# Revit family: Assa-Abloy_SecurityPortal_MP200_WallHosted
name_source: partatom
category: Doors
units: mm (PartAtom-declared; Revit-internal decimal feet)

## family parameters
Always vertical = Yes
Cut with Voids When Loaded = No
Host = Wall
OmniClass Number = 23.30.10.21.14
OmniClass Title = Security Doors
Room Calculation Point = No
Shared = No

## types (1)
- MP 200
    Access control/Biometrics = Yes
    AccessoryOptions = Contact manufacturer
    AlternativeDoorsetGlazing = Part of glazing spec
    Analytic Construction = <None>
    Anti-tailgating/Anti-piggybacking = Yes
    AntiFingerTrapRequirement = No
    BreakoutFacility = No
    Burglar resistance = EN 1627 class RC2/RC3
    CanopyHeightOptions = 250 - 1000 mm
    Capacity = 1 x 5 - 7
    Colour = Customer specific
    Configuration = 2 leafs
    Construction Type = Security Portal for controlled access
    Define Thermal Properties by = Schematic Type
    Description = Security Portal for controlled access, including high level TOF-3D sensor technology, burlgar resistance class RC2/RC3
    DiameterOptions = 1600-2500mm
    DoorIncluded = Yes
    DoorSeal = Yes
    DoorWingOptions = 2 wings
    DoorsetFasteners = Screws
    DoorsetOperation = Automatic
    DoorsetOptions = Sliding door system
    DrumWallOptions = Glass, Sandwich panel
    ElectronicLock = No
    Finish = Powder coated, Anodized, stainless steel, customer specific
    FireExit = No
    Frame Material = Aluminium
    FrameFinishOptions = Powder coated, Anodized, Clad in stainless steel, etc.
    FrameProfile = Aluminium
    FrameSeal = Yes
    Function = Exterior
    GlassLayers = 0
    GlassThickness1 = 10 mm  [stored 0.0328084 ft]
    GlassThickness2 = 10 mm  [stored 0.0328084 ft]
    GlassType = Part of glazing spec
    HandicapAccessible = Yes
    HasDrive = Yes
    HeightUnderCanopyOptions = Passage height: 2200 - 2600 mm
    Infiltration = 0
    IsExternal = Yes
    LeafColourOptions = All RAL, customer specific
    Manufacturer = Assa Abloy Entrance Systems
    ManufacturerURL = www.assaabloyentrance.com
    Material = Aluminium
    Model = Security Portal MP 200
    ModelReference = Depends on the configuration
    NominalHeight = 3250 mm
    NominalLength = 1800 mm  [stored 5.90551 ft]
    NominalWidth = 1800 mm  [stored 5.90551 ft]
    OperatingTemperature = -15º to +50ºC
    PassageWidthOptions = Depends on diameter, 1005 - 1619 mm
    ReferenceStandard = EN16005, EN16361, DIN 18650, etc.
    ReplacementCost = Depends on the configuration and door type
    SafetyDevices = Fully compliant with EN16005, Safety buffers, Presence sensors, etc.
    SelfClosing = Yes
    ServiceLifeDuration = 10-15 years
    Shape = Cylinder shaped
    SmokeStop = No
    ThermalTransmittance = 0
    ThresholdRequired = No
    ThresholdStripping = No
    URL = www.assaabloyentrance.com
    Uniclass2 = Ss_25_30_20_70
    Wall Closure = By host
    WarrantyDescription = Depends on country
    WarrantyDurationLabor = Depends on country
    WarrantyDurationParts = Depends on country
    WarrantyGuarantorLabor = Local door manufacturer
    WarrantyGuarantorParts = Local door manufacturer
    WarrantyStartDate = Depends on country
    Weight = Depends on configuration and size
    version = Version 1.0

note: [stored X ft] marks values corroborated as IEEE doubles in the binary element streams (Revit-internal decimal feet)

## geometry (parser evidence)
native form markers: Sweep x46
no freeform markers — native parametric forms only
